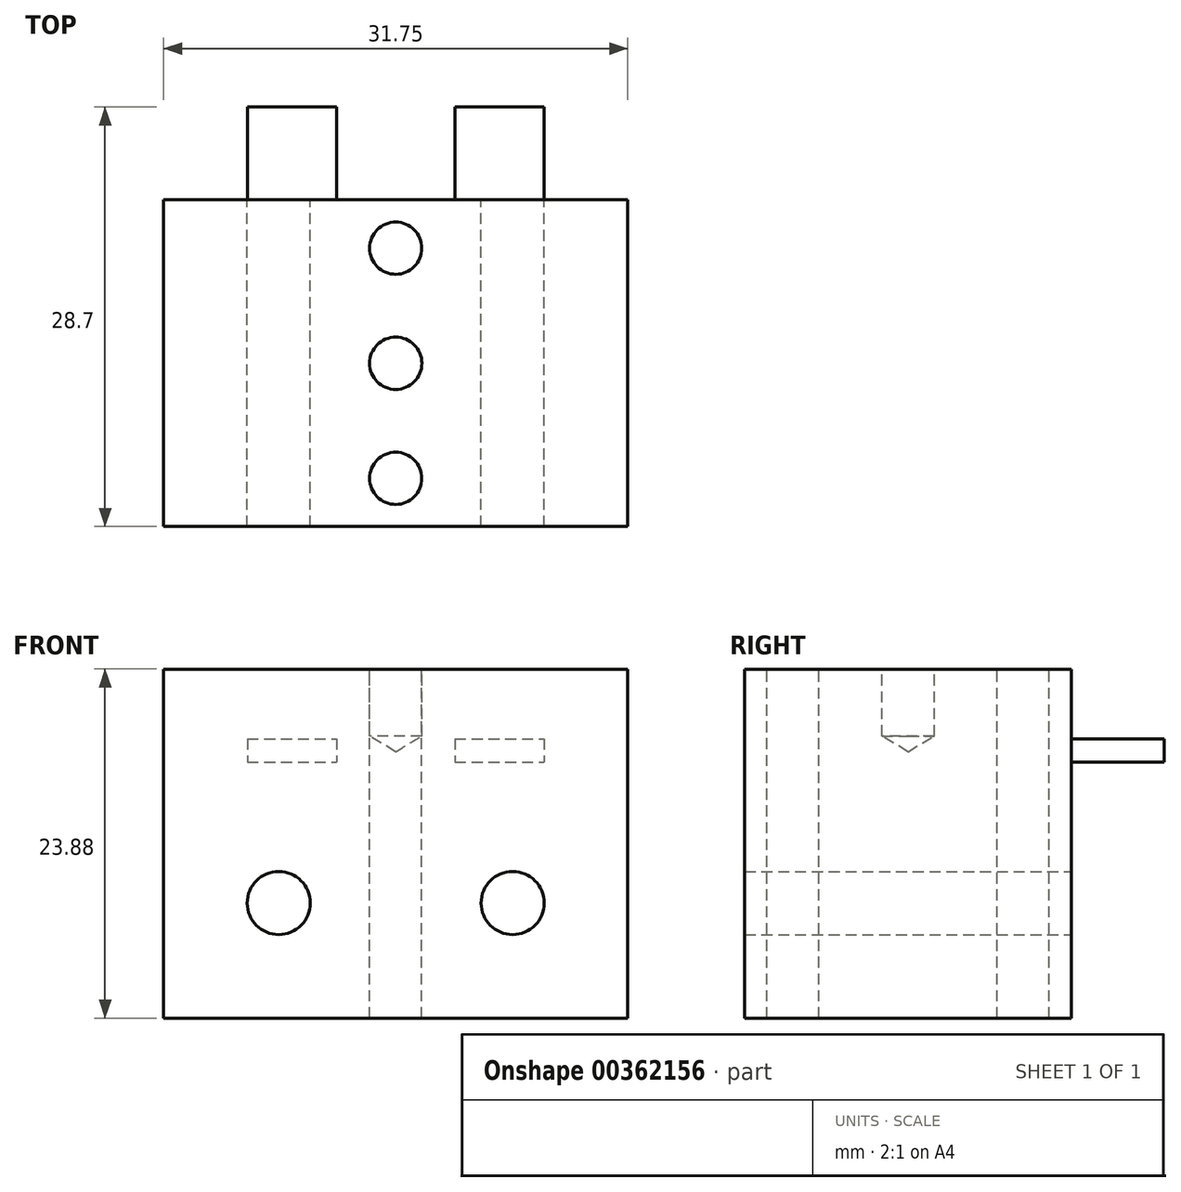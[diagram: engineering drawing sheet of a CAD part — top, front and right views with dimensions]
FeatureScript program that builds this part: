
annotation { "Feature Type Name" : "Feature", "Feature Type Description" : "" }
export const myFeature = defineFeature(function(context is Context, id is Id, definition is map)
    precondition{}
    {
        {
            var Q0;
            Q0=qCreatedBy(makeId("Front.planeOp"),FACE);
            var sketch = newSketch(context, id + "F0", { "sketchPlane" : qUnion([Q0])});
            skLineSegment(sketch, "E0.bottom", {"start": v(0, 0) * mm, "end": v(31.75, 0) * mm});
            skLineSegment(sketch, "E0.top", {"start": v(0, 23.88) * mm, "end": v(31.75, 23.88) * mm});
            skLineSegment(sketch, "E0.left", {"start": v(0, 0) * mm, "end": v(0, 23.88) * mm});
            skLineSegment(sketch, "E0.right", {"start": v(31.75, 0) * mm, "end": v(31.75, 23.88) * mm});
            skLineSegment(sketch, "E1.bottom", {"start": v(5.73, 19.11) * mm, "end": v(11.83, 19.11) * mm});
            skLineSegment(sketch, "E1.top", {"start": v(5.73, 17.53) * mm, "end": v(11.83, 17.53) * mm});
            skLineSegment(sketch, "E1.left", {"start": v(5.73, 19.11) * mm, "end": v(5.73, 17.53) * mm});
            skLineSegment(sketch, "E1.right", {"start": v(11.83, 19.11) * mm, "end": v(11.83, 17.53) * mm});
            skLineSegment(sketch, "E2.bottom", {"start": v(19.92, 19.11) * mm, "end": v(26.02, 19.11) * mm});
            skLineSegment(sketch, "E2.top", {"start": v(19.92, 17.53) * mm, "end": v(26.02, 17.53) * mm});
            skLineSegment(sketch, "E2.left", {"start": v(19.92, 19.11) * mm, "end": v(19.92, 17.53) * mm});
            skLineSegment(sketch, "E2.right", {"start": v(26.02, 19.11) * mm, "end": v(26.02, 17.53) * mm});
            skLineSegment(sketch, "E3", {"start": v(5.73, 19.11) * mm, "end": v(5.73, 23.88) * mm, "construction": true});
            skLineSegment(sketch, "E4", {"start": v(26.02, 19.11) * mm, "end": v(26.02, 23.88) * mm, "construction": true});
            skLineSegment(sketch, "E5", {"start": v(26.02, 19.11) * mm, "end": v(31.75, 19.11) * mm, "construction": true});
            skLineSegment(sketch, "E6", {"start": v(5.73, 19.11) * mm, "end": v(0, 19.11) * mm, "construction": true});
            skLineSegment(sketch, "E7", {"start": v(0, 7.87) * mm, "end": v(7.87, 7.87) * mm, "construction": true});
            skLineSegment(sketch, "E8", {"start": v(7.87, 7.87) * mm, "end": v(23.88, 7.87) * mm, "construction": true});
            skLineSegment(sketch, "E9", {"start": v(23.88, 7.87) * mm, "end": v(31.75, 7.87) * mm, "construction": true});
            skLineSegment(sketch, "E10", {"start": v(23.88, 7.87) * mm, "end": v(23.88, 0) * mm, "construction": true});
            skPoint(sketch, "E11", {"position": v(7.87, 7.87) * mm});
            skPoint(sketch, "E12", {"position": v(23.88, 7.87) * mm});
            skSolve(sketch);
        }
        {
            var Q0;
            Q0=makeQuery(id+"F0.imprint","IMPRINT",FACE,{"disambiguationData":[TD([[makeQuery(id+"F0.imprint","IMPRINT",EDGE,{"derivedFrom":sQuery(id+"F0.wireOp",EDGE,"E0.bottom")}),1.0]])]});
            var Q1;
            Q1=makeQuery(id+"F0.imprint","IMPRINT",FACE,{"disambiguationData":[TD([[makeQuery(id+"F0.imprint","IMPRINT",EDGE,{"derivedFrom":sQuery(id+"F0.wireOp",EDGE,"E1.bottom")}),-1.0]])]});
            var Q2;
            Q2=makeQuery(id+"F0.imprint","IMPRINT",FACE,{"disambiguationData":[TD([[makeQuery(id+"F0.imprint","IMPRINT",EDGE,{"derivedFrom":sQuery(id+"F0.wireOp",EDGE,"E2.bottom")}),-1.0]])]});
            extrude(context, id + "F1", {"entities" : qUnion([Q0, Q1, Q2]), "depth" : 22.35 * mm});
        }
        {
            var Q0;
            Q0=makeQuery(id+"F0.imprint","IMPRINT",FACE,{"disambiguationData":[TD([[makeQuery(id+"F0.imprint","IMPRINT",EDGE,{"derivedFrom":sQuery(id+"F0.wireOp",EDGE,"E2.bottom")}),-1.0]])]});
            var Q1;
            Q1=makeQuery(id+"F0.imprint","IMPRINT",FACE,{"disambiguationData":[TD([[makeQuery(id+"F0.imprint","IMPRINT",EDGE,{"derivedFrom":sQuery(id+"F0.wireOp",EDGE,"E1.bottom")}),-1.0]])]});
            extrude(context, id + "F2", {"entities" : qUnion([Q0, Q1]), "operationType" : NewBodyOperationType.ADD, "oppositeDirection" : true, "depth" : 6.35 * mm});
        }
        {
            var Q0;
            Q0=sQuery(id+"F0.wireOp",VERTEX,"E11");
            var Q1;
            Q1=sQuery(id+"F0.wireOp",VERTEX,"E12");
            var Q2;
            Q2=makeQuery(id+"F1.opExtrude","SWEPT_BODY",BODY,{"disambiguationData":[OSD([sQuery(id+"F0.wireOp",EDGE,"E0.bottom"),sQuery(id+"F0.wireOp",EDGE,"E0.top"),sQuery(id+"F0.wireOp",EDGE,"E0.left"),sQuery(id+"F0.wireOp",EDGE,"E0.right")])]});
            hole(context, id + "F3", {"style" : HoleStyle.SIMPLE, "endStyle" : HoleEndStyle.THROUGH, "oppositeDirection" : true, "holeDiameter" : 4.32 * mm, "isTappedThrough" : true, "tappedDepth" : 12.7 * mm, "tapClearance" : 3, "startFromSketch" : true, "locations" : qUnion([Q0, Q1]), "scope" : qUnion([Q2])});
        }
        {
            var Q0;
            Q0=makeQuery(id+"F1.opExtrude","SWEPT_FACE",FACE,{"disambiguationData":[OSD([sQuery(id+"F0.wireOp",EDGE,"E0.top")])]});
            var sketch = newSketch(context, id + "F4", { "sketchPlane" : qUnion([Q0])});
            skLineSegment(sketch, "E13", {"start": v(15.88, 0) * mm, "end": v(15.88, -3.3) * mm, "construction": true});
            skLineSegment(sketch, "E14", {"start": v(15.88, -3.3) * mm, "end": v(15.88, -19.05) * mm, "construction": true});
            skLineSegment(sketch, "E15", {"start": v(15.88, -19.05) * mm, "end": v(15.88, -22.35) * mm, "construction": true});
            skPoint(sketch, "E16", {"position": v(15.88, -3.3) * mm});
            skPoint(sketch, "E17", {"position": v(15.88, -19.05) * mm});
            skPoint(sketch, "E18", {"position": v(15.88, -11.18) * mm});
            skSolve(sketch);
        }
        {
            var Q0;
            Q0=sQuery(id+"F4.wireOp",VERTEX,"E16");
            var Q1;
            Q1=sQuery(id+"F4.wireOp",VERTEX,"E17");
            var Q2;
            Q2=makeQuery(id+"F1.opExtrude","SWEPT_BODY",BODY,{"disambiguationData":[OSD([sQuery(id+"F0.wireOp",EDGE,"E0.bottom"),sQuery(id+"F0.wireOp",EDGE,"E0.top"),sQuery(id+"F0.wireOp",EDGE,"E0.left"),sQuery(id+"F0.wireOp",EDGE,"E0.right")])]});
            hole(context, id + "F5", {"style" : HoleStyle.SIMPLE, "endStyle" : HoleEndStyle.THROUGH, "holeDiameter" : 3.57 * mm, "isTappedThrough" : true, "tappedDepth" : 12.7 * mm, "tapClearance" : 3, "startFromSketch" : true, "locations" : qUnion([Q0, Q1]), "scope" : qUnion([Q2])});
        }
        {
            var Q0;
            Q0=sQuery(id+"F4.wireOp",VERTEX,"E18");
            var Q1;
            Q1=makeQuery(id+"F1.opExtrude","SWEPT_BODY",BODY,{"disambiguationData":[OSD([sQuery(id+"F0.wireOp",EDGE,"E0.bottom"),sQuery(id+"F0.wireOp",EDGE,"E0.top"),sQuery(id+"F0.wireOp",EDGE,"E0.left"),sQuery(id+"F0.wireOp",EDGE,"E0.right")])]});
            hole(context, id + "F6", {"style" : HoleStyle.SIMPLE, "endStyle" : HoleEndStyle.BLIND, "holeDiameter" : 3.58 * mm, "holeDepth" : 4.57 * mm, "isTappedThrough" : true, "tappedDepth" : 12.7 * mm, "tapClearance" : 3, "startFromSketch" : true, "locations" : qUnion([Q0]), "scope" : qUnion([Q1])});
        }
    });
